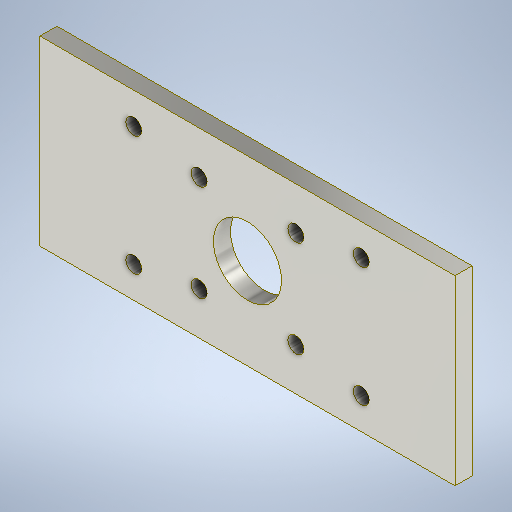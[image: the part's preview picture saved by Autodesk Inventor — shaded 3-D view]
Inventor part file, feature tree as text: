
AUTODESK INVENTOR PART (.ipt)
format: ipt  version: 2025.1 (Build 291241000, 241)  size: 236,544 bytes
history: native  units: mm
features: extrude x2, sketch x2
ambient origin geometry x8: Origin, YZ Plane, XZ Plane, XY Plane, X Axis, Y Axis, Z Axis, Center Point
bodies: Solid1 (feature_tree)
feature tree (4):
  extrude  "Extrusion1"  Depth=48.015mm
  extrude  "Extrusion2"  Depth=10.0mm
  sketch  "Sketch1"  dims[d3=0.0mm d4=48.015mm]
  sketch  "Sketch2"  dims[d5=30.0mm d6=4.007mm d7=4.5mm d8=2.8mm d9=2.8mm d10=6.5mm d11=15.507mm d12=10.0mm d13=0.0mm d14=12.0mm]
